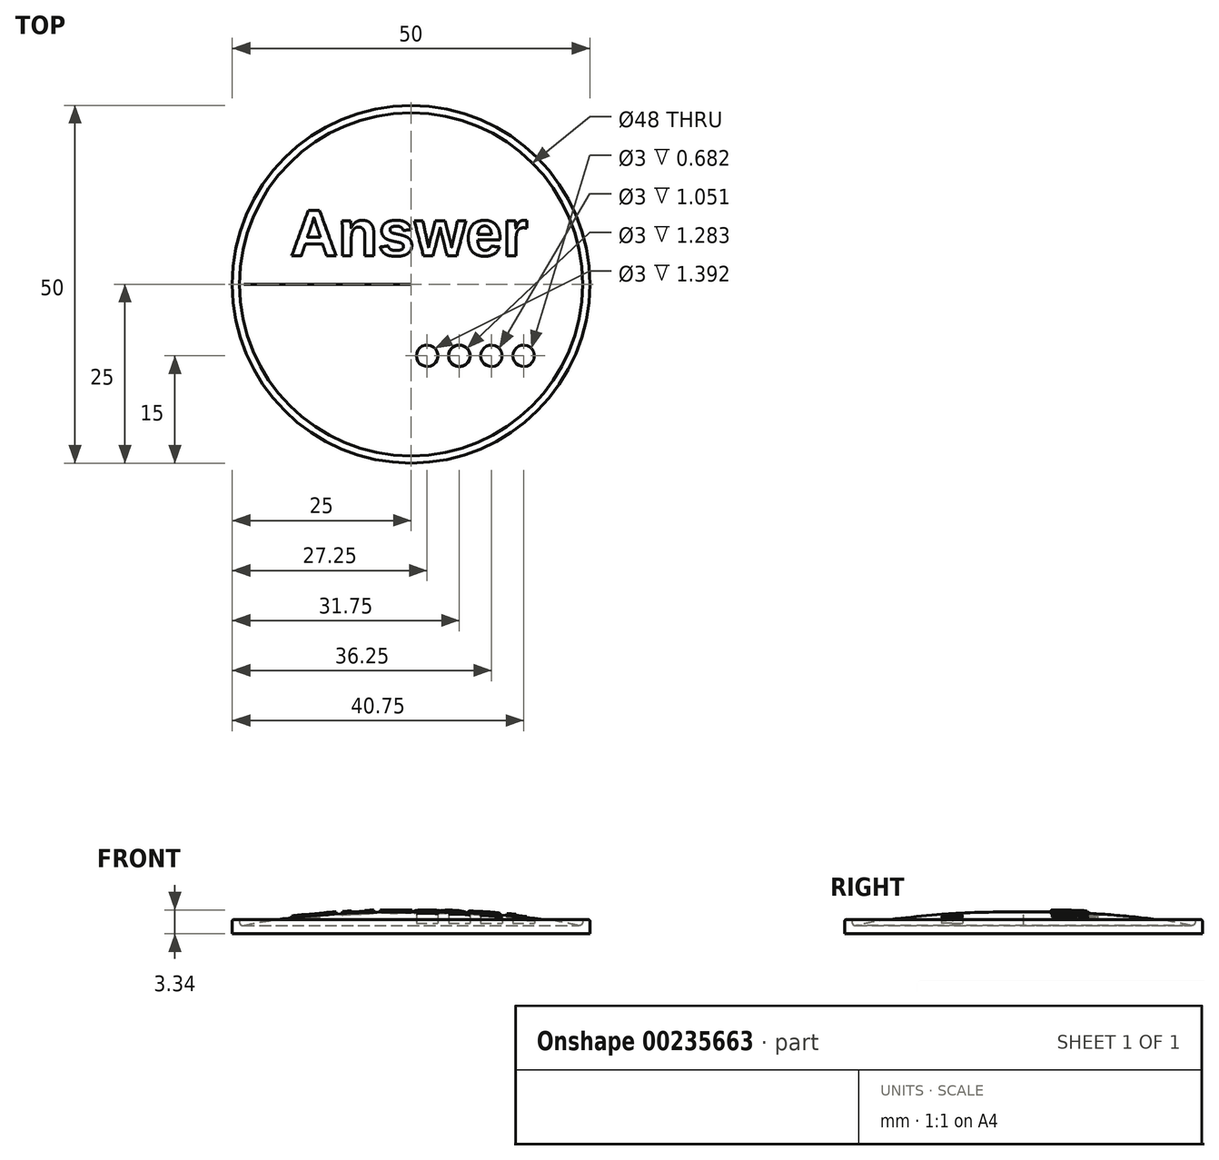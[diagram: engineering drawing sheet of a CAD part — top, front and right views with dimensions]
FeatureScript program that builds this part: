
annotation { "Feature Type Name" : "Feature", "Feature Type Description" : "" }
export const myFeature = defineFeature(function(context is Context, id is Id, definition is map)
    precondition{}
    {
        {
            var Q0;
            Q0=qCreatedBy(makeId("Top.planeOp"),FACE);
            var sketch = newSketch(context, id + "F0", { "sketchPlane" : qUnion([Q0])});
            skCircle(sketch, "E0", {"center": v(0, 0) * mm, "radius": 25 * mm});
            skCircle(sketch, "E1", {"center": v(0, 0) * mm, "radius": 24 * mm});
            skLineSegment(sketch, "E2", {"start": v(0, 0) * mm, "end": v(0, 24) * mm, "construction": true});
            skLineSegment(sketch, "E3", {"start": v(0, 0) * mm, "end": v(0, -24) * mm, "construction": true});
            skCircle(sketch, "E4", {"center": v(2.25, -10) * mm, "radius": 1.5 * mm});
            skCircle(sketch, "E5.1.0.0", {"center": v(6.75, -10) * mm, "radius": 1.5 * mm});
            skCircle(sketch, "E5.2.0.0", {"center": v(11.25, -10) * mm, "radius": 1.5 * mm});
            skCircle(sketch, "E5.3.0.0", {"center": v(15.75, -10) * mm, "radius": 1.5 * mm});
            skLineSegment(sketch, "E5.direction1", {"start": v(3.75, -10) * mm, "end": v(6.75, -10) * mm, "construction": true});
            skCircle(sketch, "E6.MirrorC", {"center": v(-2.25, -10) * mm, "radius": 1.5 * mm});
            skCircle(sketch, "E7.MirrorC", {"center": v(-6.75, -10) * mm, "radius": 1.5 * mm});
            skCircle(sketch, "E8.MirrorC", {"center": v(-11.25, -10) * mm, "radius": 1.5 * mm});
            skCircle(sketch, "E9.MirrorC", {"center": v(-15.75, -10) * mm, "radius": 1.5 * mm});
            skText(sketch, "E10", { "text": "Answer", "fontName": "Arimo-Bold.ttf"});
            const initialGuessF0  = {"E10": [-0.0169, 0.004, 1, 0, 0.00663]};
            skSetInitialGuess(sketch, initialGuessF0);
            skSolve(sketch);
        }
        {
            var Q0;
            Q0=qCreatedBy(makeId("Front.planeOp"),FACE);
            var sketch = newSketch(context, id + "F1", { "sketchPlane" : qUnion([Q0])});
            skLineSegment(sketch, "E11.0", {"start": v(-24, 0) * mm, "end": v(24, 0) * mm});
            skLineSegment(sketch, "E12.0", {"start": v(-25, 0) * mm, "end": v(25, 0) * mm});
            skLineSegment(sketch, "E13", {"start": v(-25, 0) * mm, "end": v(-25, 1.8) * mm});
            skLineSegment(sketch, "E14", {"start": v(-24.8, 2) * mm, "end": v(-24.2, 2) * mm});
            skLineSegment(sketch, "E15", {"start": v(-24, 1.8) * mm, "end": v(-24, 1.66) * mm});
            skLineSegment(sketch, "E16", {"start": v(0, 0) * mm, "end": v(0, 3) * mm});
            skFitSpline(sketch, "E17", {"points": [v(-24, 1) * mm, v(0, 3) * mm], "startDerivative": vector(10.42, 3.22) * mm, "endDerivative": vector(24.57, -1.03) * mm});
            skArc(sketch, "E18.filletArc", {"start": v(-24, 1.66) * mm, "mid": v(-23.8, 1.26) * mm, "end": v(-23.38, 1.17) * mm});
            skPoint(sketch, "E19.visualSharp", {"position": v(-25, 2) * mm});
            skArc(sketch, "E19.filletArc", {"start": v(-24.8, 2) * mm, "mid": v(-24.94, 1.94) * mm, "end": v(-25, 1.8) * mm});
            skPoint(sketch, "E20.visualSharp", {"position": v(-24, 2) * mm});
            skArc(sketch, "E20.filletArc", {"start": v(-24, 1.8) * mm, "mid": v(-24.06, 1.94) * mm, "end": v(-24.2, 2) * mm});
            skLineSegment(sketch, "E21", {"start": v(-23.38, 1.17) * mm, "end": v(-23.38, 2.85) * mm, "construction": true});
            skLineSegment(sketch, "E22", {"start": v(0, 3) * mm, "end": v(0, 5.02) * mm, "construction": true});
            skPoint(sketch, "E23", {"position": v(0, 3.2) * mm});
            skPoint(sketch, "E24", {"position": v(-23.38, 1.37) * mm});
            skFitSpline(sketch, "E25", {"points": [v(-23.38, 1.37) * mm, v(0, 3.2) * mm], "startDerivative": vector(11.8, 3.63) * mm, "endDerivative": vector(21, -1.68) * mm});
            skLineSegment(sketch, "E26", {"start": v(-23.38, 1.37) * mm, "end": v(-23.38, 7.11) * mm});
            skPoint(sketch, "E26.endSnap0", {"position": v(-23.38, 2.01) * mm});
            skLineSegment(sketch, "E27", {"start": v(0, 3.2) * mm, "end": v(0, 7.11) * mm});
            skLineSegment(sketch, "E28", {"start": v(0, 7.11) * mm, "end": v(-23.38, 7.11) * mm});
            skSolve(sketch);
        }
        {
            var Q0;
            Q0=qCreatedBy(makeId("Top.planeOp"),FACE);
            cPlane(context, id + "F2", {"entities" : qUnion([Q0]), "cplaneType" : CPlaneType.OFFSET, "offset" : 1.5 * mm, "width" : 150 * mm, "height" : 150 * mm});
        }
        {
            var Q0;
            Q0=qCreatedBy(id+"F2.planeOp",FACE);
            var sketch = newSketch(context, id + "F3", { "sketchPlane" : qUnion([Q0])});
            skCircle(sketch, "E29.0", {"center": v(-15.75, -10) * mm, "radius": 1.5 * mm});
            skCircle(sketch, "E30.0", {"center": v(-11.25, -10) * mm, "radius": 1.5 * mm});
            skCircle(sketch, "E31.0", {"center": v(-6.75, -10) * mm, "radius": 1.5 * mm});
            skCircle(sketch, "E32.0", {"center": v(-2.25, -10) * mm, "radius": 1.5 * mm});
            skCircle(sketch, "E33.0", {"center": v(2.25, -10) * mm, "radius": 1.5 * mm});
            skCircle(sketch, "E34.0", {"center": v(6.75, -10) * mm, "radius": 1.5 * mm});
            skCircle(sketch, "E35.0", {"center": v(11.25, -10) * mm, "radius": 1.5 * mm});
            skCircle(sketch, "E36.0", {"center": v(15.75, -10) * mm, "radius": 1.5 * mm});
            skSolve(sketch);
        }
        {
            var Q0;
            {var subQ0=sQuery(id+"F1.wireOp",EDGE,"E13");Q0=makeQuery(id+"F1.imprint","IMPRINT",FACE,{"disambiguationData":[TD([[makeQuery(id+"F1.imprint","IMPRINT",EDGE,{"derivedFrom":subQ0}),-1.0]])]});}
            var Q1;
            Q1=sQuery(id+"F1.wireOp",EDGE,"E16");
            revolve(context, id + "F4", {"entities" : qUnion([Q0]), "axis" : qUnion([Q1]), "revolveType" : RevolveType.FULL});
        }
        {
            var Q0;
            Q0=makeQuery(id+"F0.imprint","IMPRINT",FACE,{"disambiguationData":[TD([[makeQuery(id+"F0.imprint","IMPRINT",EDGE,{"derivedFrom":sQuery(id+"F0.wireOp",EDGE,"E10.sketch_text.stroke-0")}),-1.0]])]});
            var Q1;
            Q1=makeQuery(id+"F0.imprint","IMPRINT",FACE,{"disambiguationData":[TD([[makeQuery(id+"F0.imprint","IMPRINT",EDGE,{"derivedFrom":sQuery(id+"F0.wireOp",EDGE,"E10.sketch_text.stroke-15")}),-1.0]])]});
            var Q2;
            Q2=makeQuery(id+"F0.imprint","IMPRINT",FACE,{"disambiguationData":[TD([[makeQuery(id+"F0.imprint","IMPRINT",EDGE,{"derivedFrom":sQuery(id+"F0.wireOp",EDGE,"E10.sketch_text.stroke-34")}),-1.0]])]});
            var Q3;
            Q3=makeQuery(id+"F0.imprint","IMPRINT",FACE,{"disambiguationData":[TD([[makeQuery(id+"F0.imprint","IMPRINT",EDGE,{"derivedFrom":sQuery(id+"F0.wireOp",EDGE,"E10.sketch_text.stroke-63")}),-1.0]])]});
            var Q4;
            Q4=makeQuery(id+"F0.imprint","IMPRINT",FACE,{"disambiguationData":[TD([[makeQuery(id+"F0.imprint","IMPRINT",EDGE,{"derivedFrom":sQuery(id+"F0.wireOp",EDGE,"E10.sketch_text.stroke-82")}),-1.0]])]});
            var Q5;
            Q5=makeQuery(id+"F0.imprint","IMPRINT",FACE,{"disambiguationData":[TD([[makeQuery(id+"F0.imprint","IMPRINT",EDGE,{"derivedFrom":sQuery(id+"F0.wireOp",EDGE,"E10.sketch_text.stroke-100")}),-1.0]])]});
            extrude(context, id + "F5", {"entities" : qUnion([Q0, Q1, Q2, Q3, Q4, Q5]), "operationType" : NewBodyOperationType.ADD, "depth" : 5 * mm});
        }
        {
            var Q0;
            Q0=makeQuery(id+"F1.imprint","IMPRINT",FACE,{"disambiguationData":[TD([[makeQuery(id+"F1.imprint","IMPRINT",EDGE,{"derivedFrom":sQuery(id+"F1.wireOp",EDGE,"E25")}),1.0]])]});
            var Q1;
            Q1=sQuery(id+"F1.wireOp",EDGE,"E27");
            revolve(context, id + "F6", {"operationType" : NewBodyOperationType.REMOVE, "entities" : qUnion([Q0]), "axis" : qUnion([Q1]), "revolveType" : RevolveType.FULL, "oppositeDirection" : true});
        }
        {
            var Q0;
            Q0=makeQuery(id+"F3.imprint","IMPRINT",FACE,{"disambiguationData":[TD([[makeQuery(id+"F3.imprint","IMPRINT",EDGE,{"derivedFrom":sQuery(id+"F3.wireOp",EDGE,"E29.0")}),-1.0]])]});
            var Q1;
            Q1=makeQuery(id+"F3.imprint","IMPRINT",FACE,{"disambiguationData":[TD([[makeQuery(id+"F3.imprint","IMPRINT",EDGE,{"derivedFrom":sQuery(id+"F3.wireOp",EDGE,"E30.0")}),-1.0]])]});
            var Q2;
            Q2=makeQuery(id+"F3.imprint","IMPRINT",FACE,{"disambiguationData":[TD([[makeQuery(id+"F3.imprint","IMPRINT",EDGE,{"derivedFrom":sQuery(id+"F3.wireOp",EDGE,"E31.0")}),-1.0]])]});
            var Q3;
            Q3=makeQuery(id+"F3.imprint","IMPRINT",FACE,{"disambiguationData":[TD([[makeQuery(id+"F3.imprint","IMPRINT",EDGE,{"derivedFrom":sQuery(id+"F3.wireOp",EDGE,"E32.0")}),-1.0]])]});
            var Q4;
            Q4=makeQuery(id+"F3.imprint","IMPRINT",FACE,{"disambiguationData":[TD([[makeQuery(id+"F3.imprint","IMPRINT",EDGE,{"derivedFrom":sQuery(id+"F3.wireOp",EDGE,"E33.0")}),1.0]])]});
            var Q5;
            Q5=makeQuery(id+"F3.imprint","IMPRINT",FACE,{"disambiguationData":[TD([[makeQuery(id+"F3.imprint","IMPRINT",EDGE,{"derivedFrom":sQuery(id+"F3.wireOp",EDGE,"E34.0")}),1.0]])]});
            var Q6;
            Q6=makeQuery(id+"F3.imprint","IMPRINT",FACE,{"disambiguationData":[TD([[makeQuery(id+"F3.imprint","IMPRINT",EDGE,{"derivedFrom":sQuery(id+"F3.wireOp",EDGE,"E35.0")}),1.0]])]});
            var Q7;
            Q7=makeQuery(id+"F3.imprint","IMPRINT",FACE,{"disambiguationData":[TD([[makeQuery(id+"F3.imprint","IMPRINT",EDGE,{"derivedFrom":sQuery(id+"F3.wireOp",EDGE,"E36.0")}),1.0]])]});
            extrude(context, id + "F7", {"entities" : qUnion([Q0, Q1, Q2, Q3, Q4, Q5, Q6, Q7]), "operationType" : NewBodyOperationType.REMOVE, "depth" : 25 * mm});
        }
    });
